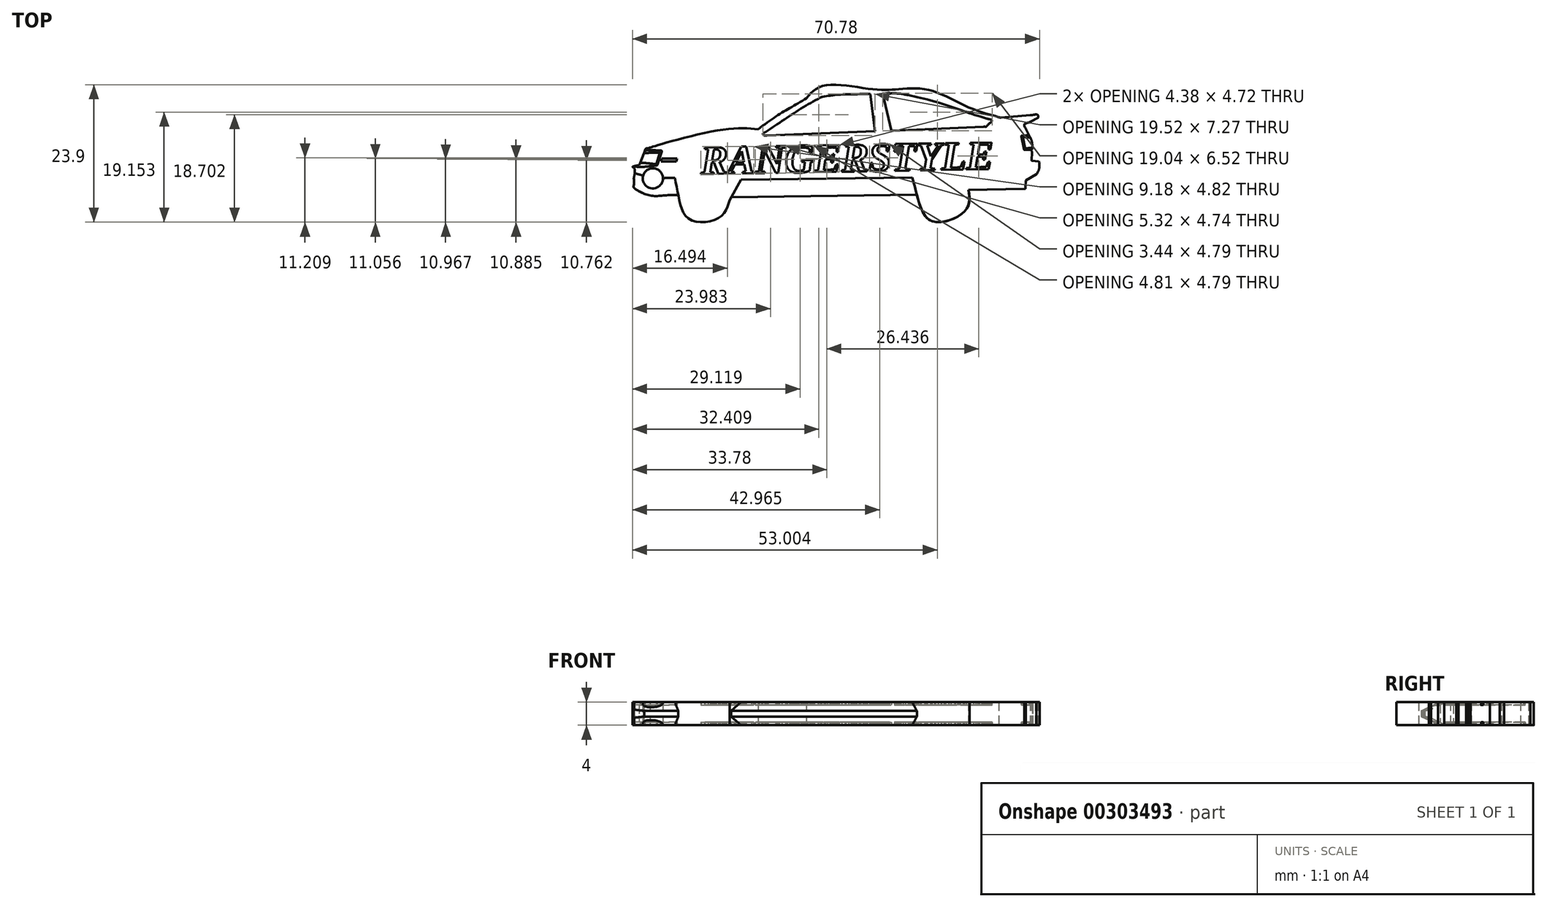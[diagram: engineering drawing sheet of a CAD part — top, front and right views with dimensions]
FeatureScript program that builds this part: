
annotation { "Feature Type Name" : "Feature", "Feature Type Description" : "" }
export const myFeature = defineFeature(function(context is Context, id is Id, definition is map)
    precondition{}
    {
        {
            var Q0;
            Q0=qCreatedBy(makeId("Top.planeOp"),FACE);
            var sketch = newSketch(context, id + "F0", { "sketchPlane" : qUnion([Q0])});
            skFitSpline(sketch, "E0", {"points": [v(-0.9, 2.52) * mm, v(-2.07, 2.25) * mm, v(-1.77, 2) * mm, v(-1.86, 0.25) * mm]});
            skFitSpline(sketch, "E1", {"points": [v(-1.86, 0.25) * mm, v(-1.81, -0.86) * mm, v(-1.9, -1.3) * mm, v(0, -2.46) * mm]});
            skFitSpline(sketch, "E2", {"points": [v(0, -2.46) * mm, v(1.87, -2.84) * mm, v(3.91, -2.69) * mm, v(5.88, -2.69) * mm]});
            skFitSpline(sketch, "E3", {"points": [v(5.88, -2.69) * mm, v(7.86, -6.9) * mm, v(13.07, -6.55) * mm, v(14.8, -3.52) * mm]});
            skLineSegment(sketch, "E4", {"start": v(-0.07, 4.59) * mm, "end": v(-0.9, 2.52) * mm});
            skLineSegment(sketch, "E5", {"start": v(-0.9, 2.52) * mm, "end": v(-0.07, 4.59) * mm});
            skFitSpline(sketch, "E6", {"points": [v(47.37, -2.6) * mm, v(50.07, -7.24) * mm, v(55.89, -5.26) * mm, v(56.36, -1.75) * mm]});
            skLineSegment(sketch, "E7", {"start": v(14.8, -3.52) * mm, "end": v(15.07, -3.04) * mm});
            skLineSegment(sketch, "E8", {"start": v(15.07, -3.04) * mm, "end": v(47.37, -2.6) * mm});
            skFitSpline(sketch, "E9", {"points": [v(66.08, -1.57) * mm, v(66.23, -1.57) * mm, v(66.24, -1.48) * mm, v(66.26, -1.37) * mm]});
            skLineSegment(sketch, "E10", {"start": v(56.36, -1.75) * mm, "end": v(66.08, -1.57) * mm});
            skLineSegment(sketch, "E11", {"start": v(66.08, -1.57) * mm, "end": v(56.36, -1.75) * mm});
            skFitSpline(sketch, "E12", {"points": [v(68.14, 0.93) * mm, v(68.57, 1.66) * mm, v(68.66, 2.26) * mm, v(68.7, 3.05) * mm]});
            skLineSegment(sketch, "E13", {"start": v(66.26, -1.37) * mm, "end": v(66.33, -0.14) * mm});
            skLineSegment(sketch, "E14", {"start": v(66.33, -0.14) * mm, "end": v(68.14, 0.93) * mm});
            skFitSpline(sketch, "E15", {"points": [v(67.4, 3.3) * mm, v(67.37, 3.3) * mm, v(67.33, 3.34) * mm, v(67.33, 3.4) * mm]});
            skLineSegment(sketch, "E16", {"start": v(68.53, 3.2) * mm, "end": v(67.4, 3.3) * mm});
            skLineSegment(sketch, "E17", {"start": v(67.4, 3.3) * mm, "end": v(68.53, 3.2) * mm});
            skFitSpline(sketch, "E18", {"points": [v(67.42, 4.77) * mm, v(67.42, 4.83) * mm, v(67.41, 4.86) * mm, v(67.37, 4.91) * mm]});
            skLineSegment(sketch, "E19", {"start": v(67.33, 3.4) * mm, "end": v(67.42, 4.77) * mm});
            skLineSegment(sketch, "E20", {"start": v(67.42, 4.77) * mm, "end": v(67.33, 3.4) * mm});
            skFitSpline(sketch, "E21", {"points": [v(67.5, 5.5) * mm, v(67.3, 6.9) * mm, v(67.02, 7.49) * mm, v(66.34, 8.87) * mm]});
            skFitSpline(sketch, "E22", {"points": [v(66.34, 8.87) * mm, v(66.08, 9.62) * mm, v(66.96, 10) * mm, v(67.98, 10.56) * mm]});
            skFitSpline(sketch, "E23", {"points": [v(67.98, 10.56) * mm, v(68.47, 10.84) * mm, v(68.38, 11.28) * mm, v(67.5, 11.25) * mm]});
            skFitSpline(sketch, "E24", {"points": [v(67.5, 11.25) * mm, v(67.43, 11.25) * mm, v(67.2, 11.25) * mm, v(67.11, 11.25) * mm]});
            skLineSegment(sketch, "E25", {"start": v(67.37, 4.91) * mm, "end": v(67.2, 5.12) * mm});
            skLineSegment(sketch, "E26", {"start": v(67.2, 5.12) * mm, "end": v(67.46, 5.4) * mm});
            skFitSpline(sketch, "E27", {"points": [v(62, 10.83) * mm, v(61.88, 10.82) * mm, v(61.77, 10.84) * mm, v(61.66, 10.88) * mm]});
            skFitSpline(sketch, "E28", {"points": [v(61.66, 10.88) * mm, v(55.86, 12.83) * mm, v(49.63, 15.6) * mm, v(44.2, 15.74) * mm]});
            skFitSpline(sketch, "E29", {"points": [v(44.2, 15.74) * mm, v(39.77, 15.73) * mm, v(31.21, 16.36) * mm, v(28.19, 14.2) * mm]});
            skFitSpline(sketch, "E30", {"points": [v(28.19, 14.2) * mm, v(25.42, 12.54) * mm, v(22.96, 11.08) * mm, v(19.79, 8.78) * mm]});
            skFitSpline(sketch, "E31", {"points": [v(19.79, 8.78) * mm, v(13.42, 8.69) * mm, v(2.09, 5.94) * mm, v(1, 5.62) * mm]});
            skFitSpline(sketch, "E32", {"points": [v(1, 5.62) * mm, v(0.46, 5.45) * mm, v(0.27, 5.45) * mm, v(-0.07, 4.59) * mm]});
            skLineSegment(sketch, "E33", {"start": v(67.11, 11.25) * mm, "end": v(62, 10.83) * mm});
            skLineSegment(sketch, "E34", {"start": v(62, 10.83) * mm, "end": v(67.11, 11.25) * mm});
            skLineSegment(sketch, "E35", {"start": v(-0.07, 4.59) * mm, "end": v(-0.07, 4.59) * mm});
            skLineSegment(sketch, "E36", {"start": v(68.53, 3.2) * mm, "end": v(68.7, 3.05) * mm});
            skLineSegment(sketch, "E37", {"start": v(67.46, 5.4) * mm, "end": v(67.5, 5.5) * mm});
            skCircle(sketch, "E38", {"center": v(1.46, 0.24) * mm, "radius": 1.75 * mm});
            skSolve(sketch);
        }
        {
            var Q0;
            Q0 = qSketchRegion(id + "F0", true);
            extrude(context, id + "F1", {"entities" : qUnion([Q0]), "depth" : 4 * mm});
        }
        {
            var Q0;
            Q0=qCreatedBy(makeId("Top.planeOp"),FACE);
            var sketch = newSketch(context, id + "F2", { "sketchPlane" : qUnion([Q0])});
            skFitSpline(sketch, "E39", {"points": [v(12.38, 5.65) * mm, v(12.69, 5.66) * mm, v(12.96, 5.64) * mm, v(13.18, 5.59) * mm]});
            skFitSpline(sketch, "E40", {"points": [v(13.18, 5.59) * mm, v(13.4, 5.55) * mm, v(13.6, 5.47) * mm, v(13.74, 5.38) * mm]});
            skFitSpline(sketch, "E41", {"points": [v(13.74, 5.38) * mm, v(13.88, 5.28) * mm, v(14, 5.16) * mm, v(14.06, 5.02) * mm]});
            skFitSpline(sketch, "E42", {"points": [v(14.06, 5.02) * mm, v(14.14, 4.88) * mm, v(14.17, 4.7) * mm, v(14.18, 4.51) * mm]});
            skFitSpline(sketch, "E43", {"points": [v(14.18, 4.51) * mm, v(14.18, 4.31) * mm, v(14.16, 4.13) * mm, v(14.1, 3.97) * mm]});
            skFitSpline(sketch, "E44", {"points": [v(14.1, 3.97) * mm, v(14.05, 3.82) * mm, v(13.97, 3.68) * mm, v(13.87, 3.56) * mm]});
            skFitSpline(sketch, "E45", {"points": [v(13.87, 3.56) * mm, v(13.77, 3.45) * mm, v(13.65, 3.35) * mm, v(13.5, 3.27) * mm]});
            skFitSpline(sketch, "E46", {"points": [v(13.5, 3.27) * mm, v(13.37, 3.2) * mm, v(13.22, 3.13) * mm, v(13.06, 3.08) * mm]});
            skLineSegment(sketch, "E47", {"start": v(11.72, 2.96) * mm, "end": v(11.46, 1.34) * mm});
            skLineSegment(sketch, "E48", {"start": v(11.46, 1.34) * mm, "end": v(12.04, 1.25) * mm});
            skLineSegment(sketch, "E49", {"start": v(12.04, 1.25) * mm, "end": v(12, 1) * mm});
            skLineSegment(sketch, "E50", {"start": v(12, 1) * mm, "end": v(9.83, 0.96) * mm});
            skLineSegment(sketch, "E51", {"start": v(9.83, 0.96) * mm, "end": v(9.87, 1.21) * mm});
            skLineSegment(sketch, "E52", {"start": v(9.87, 1.21) * mm, "end": v(10.44, 1.32) * mm});
            skLineSegment(sketch, "E53", {"start": v(10.44, 1.32) * mm, "end": v(11.06, 5.29) * mm});
            skLineSegment(sketch, "E54", {"start": v(11.06, 5.29) * mm, "end": v(10.48, 5.37) * mm});
            skLineSegment(sketch, "E55", {"start": v(10.48, 5.37) * mm, "end": v(10.52, 5.62) * mm});
            skLineSegment(sketch, "E56", {"start": v(10.52, 5.62) * mm, "end": v(12.38, 5.65) * mm});
            skFitSpline(sketch, "E57", {"points": [v(11.97, 3.35) * mm, v(12.16, 3.35) * mm, v(12.33, 3.38) * mm, v(12.48, 3.43) * mm]});
            skFitSpline(sketch, "E58", {"points": [v(12.48, 3.43) * mm, v(12.63, 3.48) * mm, v(12.75, 3.55) * mm, v(12.86, 3.64) * mm]});
            skFitSpline(sketch, "E59", {"points": [v(12.86, 3.64) * mm, v(12.96, 3.74) * mm, v(13.04, 3.85) * mm, v(13.09, 3.98) * mm]});
            skFitSpline(sketch, "E60", {"points": [v(13.09, 3.98) * mm, v(13.14, 4.12) * mm, v(13.17, 4.27) * mm, v(13.16, 4.44) * mm]});
            skFitSpline(sketch, "E61", {"points": [v(13.16, 4.44) * mm, v(13.16, 4.74) * mm, v(13.08, 4.95) * mm, v(12.94, 5.08) * mm]});
            skFitSpline(sketch, "E62", {"points": [v(12.94, 5.08) * mm, v(12.8, 5.21) * mm, v(12.6, 5.27) * mm, v(12.32, 5.27) * mm]});
            skLineSegment(sketch, "E63", {"start": v(13.06, 3.08) * mm, "end": v(13.79, 1.38) * mm});
            skLineSegment(sketch, "E64", {"start": v(13.79, 1.38) * mm, "end": v(14.3, 1.3) * mm});
            skLineSegment(sketch, "E65", {"start": v(14.3, 1.3) * mm, "end": v(14.26, 1.04) * mm});
            skLineSegment(sketch, "E66", {"start": v(14.21, 1.04) * mm, "end": v(12.88, 1.01) * mm});
            skLineSegment(sketch, "E67", {"start": v(12.88, 1.01) * mm, "end": v(12.12, 2.97) * mm});
            skLineSegment(sketch, "E68", {"start": v(12.12, 2.97) * mm, "end": v(11.72, 2.96) * mm});
            skLineSegment(sketch, "E69", {"start": v(12.32, 5.27) * mm, "end": v(12.09, 5.27) * mm});
            skLineSegment(sketch, "E70", {"start": v(12.09, 5.27) * mm, "end": v(11.78, 3.34) * mm});
            skLineSegment(sketch, "E71", {"start": v(11.78, 3.34) * mm, "end": v(11.97, 3.35) * mm});
            skLineSegment(sketch, "E72", {"start": v(15.62, 1.32) * mm, "end": v(15.58, 1.06) * mm});
            skLineSegment(sketch, "E73", {"start": v(15.58, 1.06) * mm, "end": v(14.21, 1.04) * mm});
            skLineSegment(sketch, "E74", {"start": v(14.21, 1.04) * mm, "end": v(14.26, 1.3) * mm});
            skLineSegment(sketch, "E75", {"start": v(14.26, 1.3) * mm, "end": v(14.61, 1.4) * mm});
            skLineSegment(sketch, "E76", {"start": v(14.61, 1.4) * mm, "end": v(16.85, 5.77) * mm});
            skLineSegment(sketch, "E77", {"start": v(16.85, 5.77) * mm, "end": v(17.68, 5.78) * mm});
            skLineSegment(sketch, "E78", {"start": v(17.68, 5.78) * mm, "end": v(18.64, 1.46) * mm});
            skLineSegment(sketch, "E79", {"start": v(18.64, 1.46) * mm, "end": v(19.02, 1.37) * mm});
            skLineSegment(sketch, "E80", {"start": v(19.02, 1.37) * mm, "end": v(18.97, 1.12) * mm});
            skLineSegment(sketch, "E81", {"start": v(18.97, 1.12) * mm, "end": v(17.07, 1.09) * mm});
            skLineSegment(sketch, "E82", {"start": v(17.07, 1.09) * mm, "end": v(17.12, 1.34) * mm});
            skLineSegment(sketch, "E83", {"start": v(17.12, 1.34) * mm, "end": v(17.6, 1.44) * mm});
            skLineSegment(sketch, "E84", {"start": v(17.6, 1.44) * mm, "end": v(17.36, 2.64) * mm});
            skLineSegment(sketch, "E85", {"start": v(17.36, 2.64) * mm, "end": v(15.72, 2.61) * mm});
            skLineSegment(sketch, "E86", {"start": v(15.72, 2.61) * mm, "end": v(15.1, 1.4) * mm});
            skLineSegment(sketch, "E87", {"start": v(15.1, 1.4) * mm, "end": v(15.62, 1.32) * mm});
            skLineSegment(sketch, "E88", {"start": v(16.9, 4.96) * mm, "end": v(15.91, 3) * mm});
            skLineSegment(sketch, "E89", {"start": v(15.91, 3) * mm, "end": v(17.28, 3.02) * mm});
            skLineSegment(sketch, "E90", {"start": v(17.28, 3.02) * mm, "end": v(16.9, 4.96) * mm});
            skFitSpline(sketch, "E91", {"points": [v(24.66, 3.03) * mm, v(24.65, 3.5) * mm, v(24.72, 3.9) * mm, v(24.86, 4.27) * mm]});
            skFitSpline(sketch, "E92", {"points": [v(24.86, 4.27) * mm, v(25, 4.63) * mm, v(25.2, 4.93) * mm, v(25.47, 5.18) * mm]});
            skFitSpline(sketch, "E93", {"points": [v(25.47, 5.18) * mm, v(25.73, 5.43) * mm, v(26.04, 5.62) * mm, v(26.4, 5.76) * mm]});
            skFitSpline(sketch, "E94", {"points": [v(26.4, 5.76) * mm, v(26.76, 5.9) * mm, v(27.15, 5.96) * mm, v(27.56, 5.97) * mm]});
            skFitSpline(sketch, "E95", {"points": [v(27.56, 5.97) * mm, v(27.88, 5.97) * mm, v(28.18, 5.96) * mm, v(28.44, 5.93) * mm]});
            skFitSpline(sketch, "E96", {"points": [v(28.44, 5.93) * mm, v(28.7, 5.9) * mm, v(28.96, 5.85) * mm, v(29.21, 5.78) * mm]});
            skLineSegment(sketch, "E97", {"start": v(23.49, 5.5) * mm, "end": v(22.88, 5.58) * mm});
            skLineSegment(sketch, "E98", {"start": v(22.88, 5.58) * mm, "end": v(22.92, 5.84) * mm});
            skLineSegment(sketch, "E99", {"start": v(22.92, 5.84) * mm, "end": v(24.57, 5.86) * mm});
            skLineSegment(sketch, "E100", {"start": v(24.57, 5.86) * mm, "end": v(24.53, 5.61) * mm});
            skLineSegment(sketch, "E101", {"start": v(24.53, 5.61) * mm, "end": v(23.92, 5.51) * mm});
            skLineSegment(sketch, "E102", {"start": v(23.92, 5.51) * mm, "end": v(23.24, 1.2) * mm});
            skLineSegment(sketch, "E103", {"start": v(23.24, 1.2) * mm, "end": v(22.84, 1.19) * mm});
            skLineSegment(sketch, "E104", {"start": v(22.84, 1.19) * mm, "end": v(20.9, 5) * mm});
            skLineSegment(sketch, "E105", {"start": v(20.9, 5) * mm, "end": v(20.34, 1.5) * mm});
            skLineSegment(sketch, "E106", {"start": v(20.34, 1.5) * mm, "end": v(20.94, 1.4) * mm});
            skLineSegment(sketch, "E107", {"start": v(20.94, 1.4) * mm, "end": v(20.9, 1.15) * mm});
            skLineSegment(sketch, "E108", {"start": v(20.9, 1.15) * mm, "end": v(19.25, 1.13) * mm});
            skLineSegment(sketch, "E109", {"start": v(19.25, 1.13) * mm, "end": v(19.3, 1.38) * mm});
            skLineSegment(sketch, "E110", {"start": v(19.3, 1.38) * mm, "end": v(19.9, 1.48) * mm});
            skLineSegment(sketch, "E111", {"start": v(19.9, 1.48) * mm, "end": v(20.53, 5.45) * mm});
            skLineSegment(sketch, "E112", {"start": v(20.53, 5.45) * mm, "end": v(19.95, 5.53) * mm});
            skLineSegment(sketch, "E113", {"start": v(19.95, 5.53) * mm, "end": v(19.99, 5.78) * mm});
            skLineSegment(sketch, "E114", {"start": v(19.99, 5.78) * mm, "end": v(21.49, 5.81) * mm});
            skLineSegment(sketch, "E115", {"start": v(21.49, 5.81) * mm, "end": v(23.05, 2.74) * mm});
            skLineSegment(sketch, "E116", {"start": v(23.05, 2.74) * mm, "end": v(23.49, 5.5) * mm});
            skFitSpline(sketch, "E117", {"points": [v(28.74, 5.31) * mm, v(28.6, 5.4) * mm, v(28.45, 5.48) * mm, v(28.26, 5.53) * mm]});
            skFitSpline(sketch, "E118", {"points": [v(28.26, 5.53) * mm, v(28.07, 5.59) * mm, v(27.86, 5.61) * mm, v(27.63, 5.6) * mm]});
            skFitSpline(sketch, "E119", {"points": [v(27.63, 5.6) * mm, v(27.37, 5.6) * mm, v(27.12, 5.54) * mm, v(26.9, 5.42) * mm]});
            skFitSpline(sketch, "E120", {"points": [v(26.9, 5.42) * mm, v(26.66, 5.3) * mm, v(26.46, 5.14) * mm, v(26.28, 4.91) * mm]});
            skFitSpline(sketch, "E121", {"points": [v(26.28, 4.91) * mm, v(26.1, 4.7) * mm, v(25.97, 4.42) * mm, v(25.87, 4.1) * mm]});
            skFitSpline(sketch, "E122", {"points": [v(25.87, 4.1) * mm, v(25.77, 3.77) * mm, v(25.73, 3.4) * mm, v(25.73, 2.98) * mm]});
            skFitSpline(sketch, "E123", {"points": [v(25.73, 2.98) * mm, v(25.74, 2.74) * mm, v(25.77, 2.53) * mm, v(25.83, 2.35) * mm]});
            skFitSpline(sketch, "E124", {"points": [v(25.83, 2.35) * mm, v(25.89, 2.16) * mm, v(25.97, 2.01) * mm, v(26.07, 1.9) * mm]});
            skFitSpline(sketch, "E125", {"points": [v(26.07, 1.9) * mm, v(26.17, 1.77) * mm, v(26.3, 1.69) * mm, v(26.43, 1.63) * mm]});
            skFitSpline(sketch, "E126", {"points": [v(26.43, 1.63) * mm, v(26.57, 1.57) * mm, v(26.72, 1.54) * mm, v(26.9, 1.55) * mm]});
            skFitSpline(sketch, "E127", {"points": [v(26.9, 1.55) * mm, v(27.07, 1.55) * mm, v(27.23, 1.57) * mm, v(27.37, 1.6) * mm]});
            skFitSpline(sketch, "E128", {"points": [v(27.37, 1.6) * mm, v(27.52, 1.64) * mm, v(27.63, 1.68) * mm, v(27.71, 1.7) * mm]});
            skLineSegment(sketch, "E129", {"start": v(29.21, 5.78) * mm, "end": v(29.04, 4.71) * mm});
            skLineSegment(sketch, "E130", {"start": v(29.04, 4.71) * mm, "end": v(28.75, 4.7) * mm});
            skLineSegment(sketch, "E131", {"start": v(28.75, 4.7) * mm, "end": v(28.74, 5.31) * mm});
            skFitSpline(sketch, "E132", {"points": [v(28.7, 1.53) * mm, v(28.55, 1.48) * mm, v(28.4, 1.44) * mm, v(28.25, 1.4) * mm]});
            skFitSpline(sketch, "E133", {"points": [v(28.25, 1.4) * mm, v(28.1, 1.35) * mm, v(27.94, 1.32) * mm, v(27.78, 1.29) * mm]});
            skFitSpline(sketch, "E134", {"points": [v(27.78, 1.29) * mm, v(27.62, 1.26) * mm, v(27.45, 1.23) * mm, v(27.28, 1.22) * mm]});
            skFitSpline(sketch, "E135", {"points": [v(27.28, 1.22) * mm, v(27.1, 1.2) * mm, v(26.93, 1.2) * mm, v(26.74, 1.19) * mm]});
            skFitSpline(sketch, "E136", {"points": [v(26.74, 1.19) * mm, v(26.41, 1.18) * mm, v(26.12, 1.22) * mm, v(25.86, 1.3) * mm]});
            skFitSpline(sketch, "E137", {"points": [v(25.86, 1.3) * mm, v(25.6, 1.38) * mm, v(25.39, 1.5) * mm, v(25.21, 1.66) * mm]});
            skFitSpline(sketch, "E138", {"points": [v(25.21, 1.66) * mm, v(25.03, 1.82) * mm, v(24.9, 2.02) * mm, v(24.8, 2.25) * mm]});
            skFitSpline(sketch, "E139", {"points": [v(24.8, 2.25) * mm, v(24.71, 2.48) * mm, v(24.66, 2.74) * mm, v(24.66, 3.03) * mm]});
            skLineSegment(sketch, "E140", {"start": v(27.71, 1.7) * mm, "end": v(27.92, 3.03) * mm});
            skLineSegment(sketch, "E141", {"start": v(27.92, 3.03) * mm, "end": v(27.34, 3.13) * mm});
            skLineSegment(sketch, "E142", {"start": v(27.34, 3.13) * mm, "end": v(27.38, 3.37) * mm});
            skLineSegment(sketch, "E143", {"start": v(27.38, 3.37) * mm, "end": v(29.45, 3.4) * mm});
            skLineSegment(sketch, "E144", {"start": v(29.45, 3.4) * mm, "end": v(29.41, 3.17) * mm});
            skLineSegment(sketch, "E145", {"start": v(29.41, 3.17) * mm, "end": v(28.95, 3.05) * mm});
            skLineSegment(sketch, "E146", {"start": v(28.95, 3.05) * mm, "end": v(28.7, 1.53) * mm});
            skFitSpline(sketch, "E147", {"points": [v(33.4, 5.59) * mm, v(33.33, 5.6) * mm, v(33.25, 5.6) * mm, v(33.15, 5.6) * mm]});
            skFitSpline(sketch, "E148", {"points": [v(33.15, 5.6) * mm, v(33.06, 5.61) * mm, v(32.96, 5.62) * mm, v(32.85, 5.62) * mm]});
            skFitSpline(sketch, "E149", {"points": [v(32.85, 5.62) * mm, v(32.75, 5.62) * mm, v(32.65, 5.62) * mm, v(32.55, 5.62) * mm]});
            skFitSpline(sketch, "E150", {"points": [v(32.55, 5.62) * mm, v(32.46, 5.62) * mm, v(32.37, 5.62) * mm, v(32.3, 5.62) * mm]});
            skLineSegment(sketch, "E151", {"start": v(29.56, 1.56) * mm, "end": v(30.17, 1.66) * mm});
            skLineSegment(sketch, "E152", {"start": v(30.17, 1.66) * mm, "end": v(30.8, 5.63) * mm});
            skLineSegment(sketch, "E153", {"start": v(30.8, 5.63) * mm, "end": v(30.22, 5.71) * mm});
            skLineSegment(sketch, "E154", {"start": v(30.22, 5.71) * mm, "end": v(30.26, 5.96) * mm});
            skLineSegment(sketch, "E155", {"start": v(30.26, 5.96) * mm, "end": v(33.9, 6.03) * mm});
            skLineSegment(sketch, "E156", {"start": v(33.9, 6.03) * mm, "end": v(33.71, 4.84) * mm});
            skLineSegment(sketch, "E157", {"start": v(33.71, 4.84) * mm, "end": v(33.4, 4.84) * mm});
            skLineSegment(sketch, "E158", {"start": v(33.4, 4.84) * mm, "end": v(33.4, 5.59) * mm});
            skFitSpline(sketch, "E159", {"points": [v(31.83, 1.73) * mm, v(31.97, 1.73) * mm, v(32.1, 1.73) * mm, v(32.23, 1.74) * mm]});
            skFitSpline(sketch, "E160", {"points": [v(32.23, 1.74) * mm, v(32.36, 1.74) * mm, v(32.47, 1.75) * mm, v(32.58, 1.76) * mm]});
            skFitSpline(sketch, "E161", {"points": [v(32.58, 1.76) * mm, v(32.68, 1.76) * mm, v(32.76, 1.77) * mm, v(32.83, 1.78) * mm]});
            skFitSpline(sketch, "E162", {"points": [v(32.83, 1.78) * mm, v(32.9, 1.79) * mm, v(32.96, 1.8) * mm, v(33, 1.8) * mm]});
            skLineSegment(sketch, "E163", {"start": v(32.3, 5.62) * mm, "end": v(31.81, 5.61) * mm});
            skLineSegment(sketch, "E164", {"start": v(31.81, 5.61) * mm, "end": v(31.54, 3.9) * mm});
            skLineSegment(sketch, "E165", {"start": v(31.54, 3.9) * mm, "end": v(32.52, 3.92) * mm});
            skLineSegment(sketch, "E166", {"start": v(32.52, 3.92) * mm, "end": v(32.7, 4.43) * mm});
            skLineSegment(sketch, "E167", {"start": v(32.7, 4.43) * mm, "end": v(33.01, 4.44) * mm});
            skLineSegment(sketch, "E168", {"start": v(33.01, 4.44) * mm, "end": v(32.79, 3) * mm});
            skLineSegment(sketch, "E169", {"start": v(32.79, 3) * mm, "end": v(32.48, 3) * mm});
            skLineSegment(sketch, "E170", {"start": v(32.48, 3) * mm, "end": v(32.45, 3.53) * mm});
            skLineSegment(sketch, "E171", {"start": v(32.45, 3.53) * mm, "end": v(31.48, 3.51) * mm});
            skLineSegment(sketch, "E172", {"start": v(31.48, 3.51) * mm, "end": v(31.2, 1.72) * mm});
            skLineSegment(sketch, "E173", {"start": v(31.2, 1.72) * mm, "end": v(31.83, 1.73) * mm});
            skLineSegment(sketch, "E174", {"start": v(33, 1.8) * mm, "end": v(33.34, 2.67) * mm});
            skLineSegment(sketch, "E175", {"start": v(33.34, 2.67) * mm, "end": v(33.66, 2.67) * mm});
            skLineSegment(sketch, "E176", {"start": v(33.66, 2.67) * mm, "end": v(33.39, 1.37) * mm});
            skLineSegment(sketch, "E177", {"start": v(33.39, 1.37) * mm, "end": v(29.52, 1.3) * mm});
            skLineSegment(sketch, "E178", {"start": v(29.52, 1.3) * mm, "end": v(29.56, 1.56) * mm});
            skLineSegment(sketch, "E179", {"start": v(-6.99, -2.04) * mm, "end": v(-6.99, -2.04) * mm});
            skLineSegment(sketch, "E180", {"start": v(31.97, 1.73) * mm, "end": v(33, 1.8) * mm});
            skFitSpline(sketch, "E181", {"points": [v(36.84, 6.08) * mm, v(37.16, 6.08) * mm, v(37.42, 6.06) * mm, v(37.65, 6.02) * mm]});
            skFitSpline(sketch, "E182", {"points": [v(37.65, 6.02) * mm, v(37.87, 5.97) * mm, v(38.06, 5.9) * mm, v(38.2, 5.8) * mm]});
            skFitSpline(sketch, "E183", {"points": [v(38.2, 5.8) * mm, v(38.35, 5.71) * mm, v(38.46, 5.6) * mm, v(38.53, 5.45) * mm]});
            skFitSpline(sketch, "E184", {"points": [v(38.53, 5.45) * mm, v(38.6, 5.3) * mm, v(38.64, 5.13) * mm, v(38.65, 4.94) * mm]});
            skFitSpline(sketch, "E185", {"points": [v(38.65, 4.94) * mm, v(38.65, 4.74) * mm, v(38.62, 4.56) * mm, v(38.57, 4.4) * mm]});
            skFitSpline(sketch, "E186", {"points": [v(38.57, 4.4) * mm, v(38.51, 4.25) * mm, v(38.44, 4.1) * mm, v(38.34, 4) * mm]});
            skFitSpline(sketch, "E187", {"points": [v(38.34, 4) * mm, v(38.24, 3.88) * mm, v(38.12, 3.78) * mm, v(37.98, 3.7) * mm]});
            skFitSpline(sketch, "E188", {"points": [v(37.98, 3.7) * mm, v(37.84, 3.62) * mm, v(37.7, 3.56) * mm, v(37.53, 3.5) * mm]});
            skLineSegment(sketch, "E189", {"start": v(36.19, 3.39) * mm, "end": v(35.93, 1.76) * mm});
            skLineSegment(sketch, "E190", {"start": v(35.93, 1.76) * mm, "end": v(36.5, 1.68) * mm});
            skLineSegment(sketch, "E191", {"start": v(36.5, 1.68) * mm, "end": v(36.47, 1.43) * mm});
            skLineSegment(sketch, "E192", {"start": v(36.47, 1.43) * mm, "end": v(34.3, 1.39) * mm});
            skLineSegment(sketch, "E193", {"start": v(34.3, 1.39) * mm, "end": v(34.34, 1.64) * mm});
            skLineSegment(sketch, "E194", {"start": v(34.34, 1.64) * mm, "end": v(34.9, 1.75) * mm});
            skLineSegment(sketch, "E195", {"start": v(34.9, 1.75) * mm, "end": v(35.53, 5.71) * mm});
            skLineSegment(sketch, "E196", {"start": v(35.53, 5.71) * mm, "end": v(34.95, 5.8) * mm});
            skLineSegment(sketch, "E197", {"start": v(34.95, 5.8) * mm, "end": v(35, 6.05) * mm});
            skLineSegment(sketch, "E198", {"start": v(35, 6.05) * mm, "end": v(36.84, 6.08) * mm});
            skFitSpline(sketch, "E199", {"points": [v(36.44, 3.77) * mm, v(36.63, 3.78) * mm, v(36.8, 3.8) * mm, v(36.95, 3.86) * mm]});
            skFitSpline(sketch, "E200", {"points": [v(36.95, 3.86) * mm, v(37.1, 3.9) * mm, v(37.22, 3.98) * mm, v(37.32, 4.07) * mm]});
            skFitSpline(sketch, "E201", {"points": [v(37.32, 4.07) * mm, v(37.43, 4.17) * mm, v(37.5, 4.28) * mm, v(37.56, 4.41) * mm]});
            skFitSpline(sketch, "E202", {"points": [v(37.56, 4.41) * mm, v(37.6, 4.55) * mm, v(37.63, 4.7) * mm, v(37.63, 4.87) * mm]});
            skFitSpline(sketch, "E203", {"points": [v(37.63, 4.87) * mm, v(37.63, 5.17) * mm, v(37.55, 5.38) * mm, v(37.4, 5.51) * mm]});
            skFitSpline(sketch, "E204", {"points": [v(37.4, 5.51) * mm, v(37.27, 5.64) * mm, v(37.06, 5.7) * mm, v(36.8, 5.7) * mm]});
            skLineSegment(sketch, "E205", {"start": v(37.53, 3.5) * mm, "end": v(38.26, 1.8) * mm});
            skLineSegment(sketch, "E206", {"start": v(38.26, 1.8) * mm, "end": v(38.77, 1.72) * mm});
            skLineSegment(sketch, "E207", {"start": v(38.77, 1.72) * mm, "end": v(38.73, 1.47) * mm});
            skLineSegment(sketch, "E208", {"start": v(38.73, 1.47) * mm, "end": v(37.34, 1.44) * mm});
            skLineSegment(sketch, "E209", {"start": v(37.34, 1.44) * mm, "end": v(36.59, 3.4) * mm});
            skLineSegment(sketch, "E210", {"start": v(36.59, 3.4) * mm, "end": v(36.19, 3.39) * mm});
            skFitSpline(sketch, "E211", {"points": [v(40.55, 1.43) * mm, v(40.24, 1.42) * mm, v(39.98, 1.44) * mm, v(39.74, 1.5) * mm]});
            skFitSpline(sketch, "E212", {"points": [v(39.74, 1.5) * mm, v(39.52, 1.54) * mm, v(39.33, 1.6) * mm, v(39.17, 1.65) * mm]});
            skLineSegment(sketch, "E213", {"start": v(36.8, 5.7) * mm, "end": v(36.55, 5.7) * mm});
            skLineSegment(sketch, "E214", {"start": v(36.55, 5.7) * mm, "end": v(36.25, 3.77) * mm});
            skLineSegment(sketch, "E215", {"start": v(36.25, 3.77) * mm, "end": v(36.44, 3.77) * mm});
            skFitSpline(sketch, "E216", {"points": [v(39.7, 2.16) * mm, v(39.74, 2.1) * mm, v(39.79, 2.05) * mm, v(39.85, 2) * mm]});
            skFitSpline(sketch, "E217", {"points": [v(39.85, 2) * mm, v(39.92, 1.96) * mm, v(39.99, 1.92) * mm, v(40.07, 1.88) * mm]});
            skFitSpline(sketch, "E218", {"points": [v(40.07, 1.88) * mm, v(40.15, 1.85) * mm, v(40.23, 1.82) * mm, v(40.32, 1.8) * mm]});
            skFitSpline(sketch, "E219", {"points": [v(40.32, 1.8) * mm, v(40.41, 1.78) * mm, v(40.5, 1.78) * mm, v(40.6, 1.78) * mm]});
            skFitSpline(sketch, "E220", {"points": [v(40.6, 1.78) * mm, v(40.78, 1.78) * mm, v(40.94, 1.8) * mm, v(41.07, 1.85) * mm]});
            skFitSpline(sketch, "E221", {"points": [v(41.07, 1.85) * mm, v(41.2, 1.89) * mm, v(41.31, 1.95) * mm, v(41.4, 2.02) * mm]});
            skFitSpline(sketch, "E222", {"points": [v(41.4, 2.02) * mm, v(41.48, 2.1) * mm, v(41.54, 2.18) * mm, v(41.58, 2.28) * mm]});
            skFitSpline(sketch, "E223", {"points": [v(41.58, 2.28) * mm, v(41.62, 2.38) * mm, v(41.64, 2.48) * mm, v(41.64, 2.6) * mm]});
            skFitSpline(sketch, "E224", {"points": [v(41.64, 2.6) * mm, v(41.64, 2.72) * mm, v(41.6, 2.83) * mm, v(41.55, 2.92) * mm]});
            skFitSpline(sketch, "E225", {"points": [v(41.55, 2.92) * mm, v(41.5, 3) * mm, v(41.42, 3.1) * mm, v(41.32, 3.16) * mm]});
            skFitSpline(sketch, "E226", {"points": [v(41.32, 3.16) * mm, v(41.23, 3.24) * mm, v(41.13, 3.3) * mm, v(41.01, 3.37) * mm]});
            skFitSpline(sketch, "E227", {"points": [v(41.01, 3.37) * mm, v(40.9, 3.43) * mm, v(40.77, 3.5) * mm, v(40.65, 3.56) * mm]});
            skFitSpline(sketch, "E228", {"points": [v(40.65, 3.56) * mm, v(40.53, 3.63) * mm, v(40.41, 3.7) * mm, v(40.3, 3.78) * mm]});
            skFitSpline(sketch, "E229", {"points": [v(40.3, 3.78) * mm, v(40.18, 3.86) * mm, v(40.07, 3.95) * mm, v(39.98, 4.05) * mm]});
            skFitSpline(sketch, "E230", {"points": [v(39.98, 4.05) * mm, v(39.89, 4.15) * mm, v(39.81, 4.27) * mm, v(39.75, 4.4) * mm]});
            skFitSpline(sketch, "E231", {"points": [v(39.75, 4.4) * mm, v(39.7, 4.54) * mm, v(39.66, 4.7) * mm, v(39.66, 4.87) * mm]});
            skFitSpline(sketch, "E232", {"points": [v(39.66, 4.87) * mm, v(39.66, 5.1) * mm, v(39.7, 5.29) * mm, v(39.77, 5.45) * mm]});
            skFitSpline(sketch, "E233", {"points": [v(39.77, 5.45) * mm, v(39.85, 5.62) * mm, v(39.97, 5.75) * mm, v(40.12, 5.87) * mm]});
            skFitSpline(sketch, "E234", {"points": [v(40.12, 5.87) * mm, v(40.28, 5.98) * mm, v(40.47, 6.06) * mm, v(40.69, 6.12) * mm]});
            skFitSpline(sketch, "E235", {"points": [v(40.69, 6.12) * mm, v(40.91, 6.18) * mm, v(41.17, 6.2) * mm, v(41.45, 6.21) * mm]});
            skFitSpline(sketch, "E236", {"points": [v(41.45, 6.21) * mm, v(41.65, 6.21) * mm, v(41.85, 6.2) * mm, v(42.05, 6.18) * mm]});
            skFitSpline(sketch, "E237", {"points": [v(42.05, 6.18) * mm, v(42.26, 6.16) * mm, v(42.45, 6.12) * mm, v(42.62, 6.08) * mm]});
            skLineSegment(sketch, "E238", {"start": v(39.17, 1.65) * mm, "end": v(39.37, 2.9) * mm});
            skLineSegment(sketch, "E239", {"start": v(39.37, 2.9) * mm, "end": v(39.68, 2.9) * mm});
            skLineSegment(sketch, "E240", {"start": v(39.68, 2.9) * mm, "end": v(39.7, 2.16) * mm});
            skFitSpline(sketch, "E241", {"points": [v(42.1, 5.65) * mm, v(42, 5.71) * mm, v(41.9, 5.76) * mm, v(41.78, 5.8) * mm]});
            skFitSpline(sketch, "E242", {"points": [v(41.78, 5.8) * mm, v(41.65, 5.84) * mm, v(41.52, 5.85) * mm, v(41.36, 5.85) * mm]});
            skFitSpline(sketch, "E243", {"points": [v(41.36, 5.85) * mm, v(41.22, 5.85) * mm, v(41.09, 5.83) * mm, v(40.98, 5.8) * mm]});
            skFitSpline(sketch, "E244", {"points": [v(40.98, 5.8) * mm, v(40.88, 5.75) * mm, v(40.8, 5.7) * mm, v(40.73, 5.65) * mm]});
            skFitSpline(sketch, "E245", {"points": [v(40.73, 5.65) * mm, v(40.66, 5.59) * mm, v(40.61, 5.52) * mm, v(40.58, 5.44) * mm]});
            skFitSpline(sketch, "E246", {"points": [v(40.58, 5.44) * mm, v(40.55, 5.36) * mm, v(40.53, 5.28) * mm, v(40.54, 5.2) * mm]});
            skFitSpline(sketch, "E247", {"points": [v(40.54, 5.2) * mm, v(40.54, 5.1) * mm, v(40.57, 5) * mm, v(40.62, 4.9) * mm]});
            skFitSpline(sketch, "E248", {"points": [v(40.62, 4.9) * mm, v(40.68, 4.82) * mm, v(40.76, 4.75) * mm, v(40.85, 4.68) * mm]});
            skFitSpline(sketch, "E249", {"points": [v(40.85, 4.68) * mm, v(40.94, 4.6) * mm, v(41.05, 4.54) * mm, v(41.17, 4.48) * mm]});
            skFitSpline(sketch, "E250", {"points": [v(41.17, 4.48) * mm, v(41.28, 4.41) * mm, v(41.4, 4.35) * mm, v(41.53, 4.28) * mm]});
            skFitSpline(sketch, "E251", {"points": [v(41.53, 4.28) * mm, v(41.65, 4.22) * mm, v(41.77, 4.14) * mm, v(41.89, 4.06) * mm]});
            skFitSpline(sketch, "E252", {"points": [v(41.89, 4.06) * mm, v(42, 3.99) * mm, v(42.11, 3.9) * mm, v(42.2, 3.8) * mm]});
            skFitSpline(sketch, "E253", {"points": [v(42.2, 3.8) * mm, v(42.3, 3.7) * mm, v(42.38, 3.58) * mm, v(42.43, 3.45) * mm]});
            skFitSpline(sketch, "E254", {"points": [v(42.43, 3.45) * mm, v(42.5, 3.32) * mm, v(42.52, 3.17) * mm, v(42.53, 3) * mm]});
            skFitSpline(sketch, "E255", {"points": [v(42.53, 3) * mm, v(42.53, 2.74) * mm, v(42.49, 2.52) * mm, v(42.4, 2.33) * mm]});
            skFitSpline(sketch, "E256", {"points": [v(42.4, 2.33) * mm, v(42.32, 2.13) * mm, v(42.2, 1.97) * mm, v(42.02, 1.84) * mm]});
            skFitSpline(sketch, "E257", {"points": [v(42.02, 1.84) * mm, v(41.85, 1.7) * mm, v(41.65, 1.6) * mm, v(41.4, 1.54) * mm]});
            skFitSpline(sketch, "E258", {"points": [v(41.4, 1.54) * mm, v(41.15, 1.47) * mm, v(40.87, 1.43) * mm, v(40.55, 1.43) * mm]});
            skLineSegment(sketch, "E259", {"start": v(42.62, 6.08) * mm, "end": v(42.44, 4.97) * mm});
            skLineSegment(sketch, "E260", {"start": v(42.44, 4.97) * mm, "end": v(42.13, 4.97) * mm});
            skLineSegment(sketch, "E261", {"start": v(42.13, 4.97) * mm, "end": v(42.1, 5.65) * mm});
            skFitSpline(sketch, "E262", {"points": [v(44.78, 5.85) * mm, v(44.73, 5.85) * mm, v(44.66, 5.85) * mm, v(44.6, 5.84) * mm]});
            skFitSpline(sketch, "E263", {"points": [v(44.6, 5.84) * mm, v(44.52, 5.84) * mm, v(44.45, 5.83) * mm, v(44.37, 5.82) * mm]});
            skFitSpline(sketch, "E264", {"points": [v(44.37, 5.82) * mm, v(44.3, 5.81) * mm, v(44.23, 5.8) * mm, v(44.17, 5.8) * mm]});
            skFitSpline(sketch, "E265", {"points": [v(44.17, 5.8) * mm, v(44.1, 5.79) * mm, v(44.04, 5.78) * mm, v(44, 5.77) * mm]});
            skLineSegment(sketch, "E266", {"start": v(43.58, 1.55) * mm, "end": v(43.61, 1.8) * mm});
            skLineSegment(sketch, "E267", {"start": v(43.61, 1.8) * mm, "end": v(44.37, 1.91) * mm});
            skLineSegment(sketch, "E268", {"start": v(44.37, 1.91) * mm, "end": v(45, 5.85) * mm});
            skLineSegment(sketch, "E269", {"start": v(45, 5.85) * mm, "end": v(44.78, 5.85) * mm});
            skFitSpline(sketch, "E270", {"points": [v(47, 5.82) * mm, v(46.96, 5.83) * mm, v(46.9, 5.84) * mm, v(46.84, 5.84) * mm]});
            skFitSpline(sketch, "E271", {"points": [v(46.84, 5.84) * mm, v(46.77, 5.85) * mm, v(46.7, 5.85) * mm, v(46.63, 5.85) * mm]});
            skFitSpline(sketch, "E272", {"points": [v(46.63, 5.85) * mm, v(46.56, 5.86) * mm, v(46.48, 5.86) * mm, v(46.4, 5.86) * mm]});
            skFitSpline(sketch, "E273", {"points": [v(46.4, 5.86) * mm, v(46.34, 5.87) * mm, v(46.27, 5.87) * mm, v(46.22, 5.87) * mm]});
            skLineSegment(sketch, "E274", {"start": v(44, 5.77) * mm, "end": v(43.76, 4.9) * mm});
            skLineSegment(sketch, "E275", {"start": v(43.76, 4.9) * mm, "end": v(43.46, 4.9) * mm});
            skLineSegment(sketch, "E276", {"start": v(43.46, 4.9) * mm, "end": v(43.66, 6.2) * mm});
            skLineSegment(sketch, "E277", {"start": v(43.66, 6.2) * mm, "end": v(47.48, 6.26) * mm});
            skLineSegment(sketch, "E278", {"start": v(47.48, 6.26) * mm, "end": v(47.28, 4.96) * mm});
            skLineSegment(sketch, "E279", {"start": v(47.28, 4.96) * mm, "end": v(46.97, 4.96) * mm});
            skLineSegment(sketch, "E280", {"start": v(46.97, 4.96) * mm, "end": v(47, 5.82) * mm});
            skLineSegment(sketch, "E281", {"start": v(46.22, 5.87) * mm, "end": v(46.02, 5.86) * mm});
            skLineSegment(sketch, "E282", {"start": v(46.02, 5.86) * mm, "end": v(45.4, 1.93) * mm});
            skLineSegment(sketch, "E283", {"start": v(45.4, 1.93) * mm, "end": v(46.11, 1.85) * mm});
            skLineSegment(sketch, "E284", {"start": v(46.11, 1.85) * mm, "end": v(46.08, 1.6) * mm});
            skLineSegment(sketch, "E285", {"start": v(46.08, 1.6) * mm, "end": v(43.58, 1.55) * mm});
            skLineSegment(sketch, "E286", {"start": v(50, 3.56) * mm, "end": v(49.76, 2) * mm});
            skLineSegment(sketch, "E287", {"start": v(49.76, 2) * mm, "end": v(50.48, 1.92) * mm});
            skLineSegment(sketch, "E288", {"start": v(50.48, 1.92) * mm, "end": v(50.44, 1.67) * mm});
            skLineSegment(sketch, "E289", {"start": v(50.44, 1.67) * mm, "end": v(47.94, 1.63) * mm});
            skLineSegment(sketch, "E290", {"start": v(47.94, 1.63) * mm, "end": v(47.98, 1.88) * mm});
            skLineSegment(sketch, "E291", {"start": v(47.98, 1.88) * mm, "end": v(48.73, 1.99) * mm});
            skLineSegment(sketch, "E292", {"start": v(48.73, 1.99) * mm, "end": v(48.98, 3.52) * mm});
            skLineSegment(sketch, "E293", {"start": v(48.98, 3.52) * mm, "end": v(48.13, 5.93) * mm});
            skLineSegment(sketch, "E294", {"start": v(48.13, 5.93) * mm, "end": v(47.62, 6.01) * mm});
            skLineSegment(sketch, "E295", {"start": v(47.62, 6.01) * mm, "end": v(47.66, 6.27) * mm});
            skLineSegment(sketch, "E296", {"start": v(47.66, 6.27) * mm, "end": v(49.86, 6.3) * mm});
            skLineSegment(sketch, "E297", {"start": v(49.86, 6.3) * mm, "end": v(49.82, 6.05) * mm});
            skLineSegment(sketch, "E298", {"start": v(49.82, 6.05) * mm, "end": v(49.18, 5.95) * mm});
            skLineSegment(sketch, "E299", {"start": v(49.18, 5.95) * mm, "end": v(49.84, 4.04) * mm});
            skLineSegment(sketch, "E300", {"start": v(49.84, 4.04) * mm, "end": v(51.06, 5.98) * mm});
            skLineSegment(sketch, "E301", {"start": v(51.06, 5.98) * mm, "end": v(50.5, 6.06) * mm});
            skLineSegment(sketch, "E302", {"start": v(50.5, 6.06) * mm, "end": v(50.55, 6.32) * mm});
            skLineSegment(sketch, "E303", {"start": v(50.55, 6.32) * mm, "end": v(52.13, 6.35) * mm});
            skLineSegment(sketch, "E304", {"start": v(52.13, 6.35) * mm, "end": v(52.09, 6.1) * mm});
            skLineSegment(sketch, "E305", {"start": v(52.09, 6.1) * mm, "end": v(51.58, 6) * mm});
            skLineSegment(sketch, "E306", {"start": v(51.58, 6) * mm, "end": v(50, 3.56) * mm});
            skFitSpline(sketch, "E307", {"points": [v(53.68, 2.1) * mm, v(53.8, 2.1) * mm, v(53.93, 2.1) * mm, v(54.07, 2.1) * mm]});
            skFitSpline(sketch, "E308", {"points": [v(54.07, 2.1) * mm, v(54.2, 2.11) * mm, v(54.34, 2.12) * mm, v(54.46, 2.13) * mm]});
            skFitSpline(sketch, "E309", {"points": [v(54.46, 2.13) * mm, v(54.58, 2.14) * mm, v(54.69, 2.15) * mm, v(54.78, 2.16) * mm]});
            skFitSpline(sketch, "E310", {"points": [v(54.78, 2.16) * mm, v(54.88, 2.17) * mm, v(54.94, 2.18) * mm, v(54.98, 2.19) * mm]});
            skLineSegment(sketch, "E311", {"start": v(54.61, 6.14) * mm, "end": v(53.92, 6.03) * mm});
            skLineSegment(sketch, "E312", {"start": v(53.92, 6.03) * mm, "end": v(53.3, 2.09) * mm});
            skLineSegment(sketch, "E313", {"start": v(53.3, 2.09) * mm, "end": v(53.68, 2.1) * mm});
            skLineSegment(sketch, "E314", {"start": v(54.98, 2.19) * mm, "end": v(55.37, 3.16) * mm});
            skLineSegment(sketch, "E315", {"start": v(55.37, 3.16) * mm, "end": v(55.66, 3.16) * mm});
            skLineSegment(sketch, "E316", {"start": v(55.66, 3.16) * mm, "end": v(55.38, 1.76) * mm});
            skLineSegment(sketch, "E317", {"start": v(55.38, 1.76) * mm, "end": v(51.62, 1.7) * mm});
            skLineSegment(sketch, "E318", {"start": v(51.62, 1.7) * mm, "end": v(51.66, 1.94) * mm});
            skLineSegment(sketch, "E319", {"start": v(51.66, 1.94) * mm, "end": v(52.27, 2.05) * mm});
            skLineSegment(sketch, "E320", {"start": v(52.27, 2.05) * mm, "end": v(52.9, 6.02) * mm});
            skLineSegment(sketch, "E321", {"start": v(52.9, 6.02) * mm, "end": v(52.32, 6.1) * mm});
            skLineSegment(sketch, "E322", {"start": v(52.32, 6.1) * mm, "end": v(52.36, 6.35) * mm});
            skLineSegment(sketch, "E323", {"start": v(52.36, 6.35) * mm, "end": v(54.66, 6.39) * mm});
            skLineSegment(sketch, "E324", {"start": v(54.66, 6.39) * mm, "end": v(54.61, 6.14) * mm});
            skFitSpline(sketch, "E325", {"points": [v(59.84, 6.05) * mm, v(59.77, 6.06) * mm, v(59.68, 6.07) * mm, v(59.59, 6.07) * mm]});
            skFitSpline(sketch, "E326", {"points": [v(59.59, 6.07) * mm, v(59.5, 6.08) * mm, v(59.4, 6.08) * mm, v(59.29, 6.08) * mm]});
            skFitSpline(sketch, "E327", {"points": [v(59.29, 6.08) * mm, v(59.19, 6.08) * mm, v(59.09, 6.08) * mm, v(58.99, 6.08) * mm]});
            skFitSpline(sketch, "E328", {"points": [v(58.99, 6.08) * mm, v(58.9, 6.08) * mm, v(58.8, 6.08) * mm, v(58.73, 6.08) * mm]});
            skLineSegment(sketch, "E329", {"start": v(56, 2.02) * mm, "end": v(56.6, 2.12) * mm});
            skLineSegment(sketch, "E330", {"start": v(56.6, 2.12) * mm, "end": v(57.23, 6.1) * mm});
            skLineSegment(sketch, "E331", {"start": v(57.23, 6.1) * mm, "end": v(56.65, 6.17) * mm});
            skLineSegment(sketch, "E332", {"start": v(56.65, 6.17) * mm, "end": v(56.7, 6.43) * mm});
            skLineSegment(sketch, "E333", {"start": v(56.7, 6.43) * mm, "end": v(60.34, 6.49) * mm});
            skLineSegment(sketch, "E334", {"start": v(60.34, 6.49) * mm, "end": v(60.15, 5.3) * mm});
            skLineSegment(sketch, "E335", {"start": v(60.15, 5.3) * mm, "end": v(59.83, 5.3) * mm});
            skLineSegment(sketch, "E336", {"start": v(59.83, 5.3) * mm, "end": v(59.84, 6.05) * mm});
            skFitSpline(sketch, "E337", {"points": [v(58.27, 2.19) * mm, v(58.4, 2.2) * mm, v(58.54, 2.2) * mm, v(58.67, 2.2) * mm]});
            skFitSpline(sketch, "E338", {"points": [v(58.67, 2.2) * mm, v(58.8, 2.2) * mm, v(58.9, 2.21) * mm, v(59.01, 2.22) * mm]});
            skFitSpline(sketch, "E339", {"points": [v(59.01, 2.22) * mm, v(59.11, 2.22) * mm, v(59.2, 2.23) * mm, v(59.27, 2.24) * mm]});
            skFitSpline(sketch, "E340", {"points": [v(59.27, 2.24) * mm, v(59.34, 2.25) * mm, v(59.4, 2.26) * mm, v(59.44, 2.26) * mm]});
            skLineSegment(sketch, "E341", {"start": v(58.73, 6.08) * mm, "end": v(58.25, 6.07) * mm});
            skLineSegment(sketch, "E342", {"start": v(58.25, 6.07) * mm, "end": v(57.98, 4.36) * mm});
            skLineSegment(sketch, "E343", {"start": v(57.98, 4.36) * mm, "end": v(58.95, 4.38) * mm});
            skLineSegment(sketch, "E344", {"start": v(58.95, 4.38) * mm, "end": v(59.14, 4.9) * mm});
            skLineSegment(sketch, "E345", {"start": v(59.14, 4.9) * mm, "end": v(59.45, 4.9) * mm});
            skLineSegment(sketch, "E346", {"start": v(59.45, 4.9) * mm, "end": v(59.22, 3.47) * mm});
            skLineSegment(sketch, "E347", {"start": v(59.22, 3.47) * mm, "end": v(58.91, 3.46) * mm});
            skLineSegment(sketch, "E348", {"start": v(58.91, 3.46) * mm, "end": v(58.89, 4) * mm});
            skLineSegment(sketch, "E349", {"start": v(58.89, 4) * mm, "end": v(57.92, 3.97) * mm});
            skLineSegment(sketch, "E350", {"start": v(57.92, 3.97) * mm, "end": v(57.63, 2.18) * mm});
            skLineSegment(sketch, "E351", {"start": v(57.63, 2.18) * mm, "end": v(58.27, 2.19) * mm});
            skLineSegment(sketch, "E352", {"start": v(59.44, 2.26) * mm, "end": v(59.78, 3.13) * mm});
            skLineSegment(sketch, "E353", {"start": v(59.78, 3.13) * mm, "end": v(60.1, 3.13) * mm});
            skLineSegment(sketch, "E354", {"start": v(60.1, 3.13) * mm, "end": v(59.82, 1.83) * mm});
            skLineSegment(sketch, "E355", {"start": v(59.82, 1.83) * mm, "end": v(55.96, 1.77) * mm});
            skLineSegment(sketch, "E356", {"start": v(55.96, 1.77) * mm, "end": v(56, 2.02) * mm});
            skLineSegment(sketch, "E357", {"start": v(19.45, -2.04) * mm, "end": v(19.45, -2.04) * mm});
            skLineSegment(sketch, "E358", {"start": v(58.4, 2.2) * mm, "end": v(59.44, 2.26) * mm});
            skSolve(sketch);
        }
        {
            var Q0;
            Q0 = qSketchRegion(id + "F2", true);
            extrude(context, id + "F3", {"entities" : qUnion([Q0]), "operationType" : NewBodyOperationType.REMOVE, "depth" : 14.4 * mm, "hasSecondDirection" : true, "secondDirectionOppositeDirection" : false, "secondDirectionDepth" : 3.5 * mm});
        }
        {
            var Q0;
            Q0=qCreatedBy(makeId("Top.planeOp"),FACE);
            var sketch = newSketch(context, id + "F4", { "sketchPlane" : qUnion([Q0])});
            skFitSpline(sketch, "E359", {"points": [v(2.26, 2.59) * mm, v(2.22, 2.5) * mm, v(2.15, 2.48) * mm, v(2.07, 2.49) * mm]});
            skFitSpline(sketch, "E360", {"points": [v(2.07, 2.49) * mm, v(-1.75, 2.4) * mm, v(-1.75, 2.77) * mm, v(2.03, 2.7) * mm]});
            skLineSegment(sketch, "E361", {"start": v(3, 4.89) * mm, "end": v(2.26, 2.59) * mm});
            skLineSegment(sketch, "E362", {"start": v(2.26, 2.59) * mm, "end": v(3, 4.89) * mm});
            skFitSpline(sketch, "E363", {"points": [v(2.67, 4.74) * mm, v(-1.35, 4.74) * mm, v(-0.2, 5.07) * mm, v(2.9, 5.05) * mm]});
            skFitSpline(sketch, "E364", {"points": [v(2.9, 5.05) * mm, v(3, 5.03) * mm, v(3.04, 4.97) * mm, v(3, 4.89) * mm]});
            skLineSegment(sketch, "E365", {"start": v(2.03, 2.7) * mm, "end": v(2.67, 4.74) * mm});
            skLineSegment(sketch, "E366", {"start": v(2.67, 4.74) * mm, "end": v(2.03, 2.7) * mm});
            skFitSpline(sketch, "E367", {"points": [v(21.1, 8.3) * mm, v(24.17, 10.37) * mm, v(27.4, 12.47) * mm, v(30.6, 14.28) * mm]});
            skFitSpline(sketch, "E368", {"points": [v(30.6, 14.28) * mm, v(30.7, 14.37) * mm, v(30.83, 14.38) * mm, v(30.95, 14.4) * mm]});
            skFitSpline(sketch, "E369", {"points": [v(30.95, 14.4) * mm, v(33.64, 14.8) * mm, v(36.46, 14.88) * mm, v(39.25, 14.95) * mm]});
            skFitSpline(sketch, "E370", {"points": [v(21.3, 7.71) * mm, v(20.84, 7.7) * mm, v(20.58, 7.98) * mm, v(21.1, 8.3) * mm]});
            skLineSegment(sketch, "E371", {"start": v(39.25, 14.95) * mm, "end": v(40.1, 8.46) * mm});
            skLineSegment(sketch, "E372", {"start": v(40.1, 8.46) * mm, "end": v(21.3, 7.71) * mm});
            skFitSpline(sketch, "E373", {"points": [v(41.41, 14.96) * mm, v(42.9, 15.02) * mm, v(44.42, 14.98) * mm, v(45.9, 14.7) * mm]});
            skFitSpline(sketch, "E374", {"points": [v(45.9, 14.7) * mm, v(50.2, 13.69) * mm, v(57.07, 11.4) * mm, v(59.57, 10.6) * mm]});
            skFitSpline(sketch, "E375", {"points": [v(59.57, 10.6) * mm, v(60.46, 10.28) * mm, v(59.93, 9.76) * mm, v(59.56, 9.38) * mm]});
            skFitSpline(sketch, "E376", {"points": [v(59.56, 9.38) * mm, v(59.4, 9.2) * mm, v(59.2, 9.24) * mm, v(58.96, 9.23) * mm]});
            skFitSpline(sketch, "E377", {"points": [v(65.68, 7.65) * mm, v(65.58, 7.65) * mm, v(65.56, 7.58) * mm, v(65.59, 7.5) * mm]});
            skLineSegment(sketch, "E378", {"start": v(58.96, 9.23) * mm, "end": v(42.95, 8.5) * mm});
            skFitSpline(sketch, "E379", {"points": [v(66.01, 5.3) * mm, v(66.04, 5.23) * mm, v(66.08, 5.2) * mm, v(66.16, 5.2) * mm]});
            skFitSpline(sketch, "E380", {"points": [v(66.16, 5.2) * mm, v(67.37, 5.26) * mm, v(67.72, 5.46) * mm, v(66.22, 5.45) * mm]});
            skLineSegment(sketch, "E381", {"start": v(65.59, 7.5) * mm, "end": v(66.01, 5.3) * mm});
            skLineSegment(sketch, "E382", {"start": v(66.01, 5.3) * mm, "end": v(65.59, 7.5) * mm});
            skFitSpline(sketch, "E383", {"points": [v(65.82, 7.45) * mm, v(67.39, 7.4) * mm, v(67.15, 7.64) * mm, v(65.68, 7.65) * mm]});
            skLineSegment(sketch, "E384", {"start": v(66.22, 5.45) * mm, "end": v(65.82, 7.45) * mm});
            skLineSegment(sketch, "E385", {"start": v(65.82, 7.45) * mm, "end": v(66.22, 5.45) * mm});
            skLineSegment(sketch, "E386", {"start": v(3.02, 3.7) * mm, "end": v(2.86, 3.18) * mm});
            skLineSegment(sketch, "E387", {"start": v(2.86, 3.18) * mm, "end": v(5.56, 3.19) * mm});
            skLineSegment(sketch, "E388", {"start": v(5.56, 3.19) * mm, "end": v(5.7, 3.7) * mm});
            skLineSegment(sketch, "E389", {"start": v(5.7, 3.7) * mm, "end": v(3.02, 3.7) * mm});
            skLineSegment(sketch, "E390", {"start": v(41.41, 14.96) * mm, "end": v(42.95, 8.5) * mm});
            skSolve(sketch);
        }
        {
            var Q0;
            Q0 = qSketchRegion(id + "F4", true);
            extrude(context, id + "F5", {"entities" : qUnion([Q0]), "operationType" : NewBodyOperationType.REMOVE, "depth" : 25 * mm, "hasSecondDirection" : true, "secondDirectionOppositeDirection" : false, "secondDirectionDepth" : 3.5 * mm});
        }
        {
            var Q0;
            Q0=makeQuery(id+"F1.opExtrude","CAP_EDGE",EDGE,{"disambiguationData":[OSD([sQuery(id+"F0.wireOp",EDGE,"E8")])],"isStart":false});
            var Q1;
            Q1=makeQuery(id+"F1.opExtrude","CAP_EDGE",EDGE,{"disambiguationData":[OSD([sQuery(id+"F0.wireOp",EDGE,"E8")])],"isStart":true});
            var Q2;
            Q2=makeQuery(id+"F1.opExtrude","CAP_EDGE",EDGE,{"disambiguationData":[OSD([sQuery(id+"F0.wireOp",EDGE,"E11")])],"isStart":false});
            var Q3;
            Q3=makeQuery(id+"F1.opExtrude","CAP_EDGE",EDGE,{"disambiguationData":[OSD([sQuery(id+"F0.wireOp",EDGE,"E11")])],"isStart":true});
            chamfer(context, id + "F6", {"entities" : qUnion([Q0, Q1, Q2, Q3]), "chamferType" : ChamferType.TWO_OFFSETS, "width1" : 3 * mm, "oppositeDirection" : false, "width2" : 1.5 * mm, "tangentPropagation" : true});
        }
        {
            var Q0;
            Q0=makeQuery(id+"F1.opExtrude","CAP_EDGE",EDGE,{"disambiguationData":[OSD([sQuery(id+"F0.wireOp",EDGE,"E2")])],"isStart":false});
            var Q1;
            Q1=makeQuery(id+"F1.opExtrude","CAP_EDGE",EDGE,{"disambiguationData":[OSD([sQuery(id+"F0.wireOp",EDGE,"E2")])],"isStart":true});
            chamfer(context, id + "F7", {"entities" : qUnion([Q0, Q1]), "chamferType" : ChamferType.TWO_OFFSETS, "width1" : 3 * mm, "oppositeDirection" : false, "width2" : 1.5 * mm, "tangentPropagation" : true});
        }
        {
            var Q0;
            Q0 = qSketchRegion(id + "F2", true);
            extrude(context, id + "F8", {"entities" : qUnion([Q0]), "operationType" : NewBodyOperationType.REMOVE, "depth" : 0.5 * mm});
        }
        {
            var Q0;
            Q0 = qSketchRegion(id + "F4", true);
            extrude(context, id + "F9", {"entities" : qUnion([Q0]), "operationType" : NewBodyOperationType.REMOVE, "depth" : 0.5 * mm});
        }
    });
